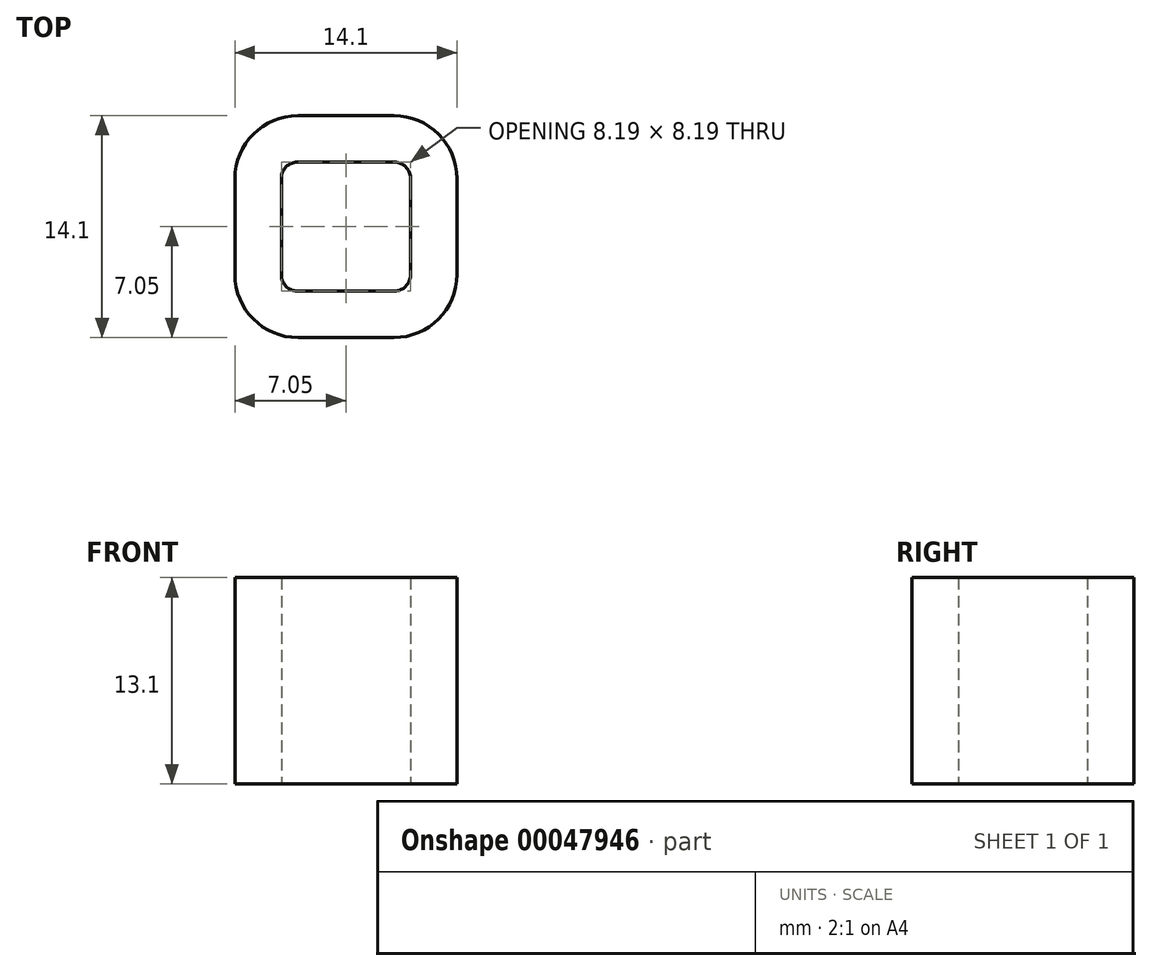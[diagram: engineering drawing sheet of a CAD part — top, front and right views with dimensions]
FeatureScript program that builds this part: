
annotation { "Feature Type Name" : "Feature", "Feature Type Description" : "" }
export const myFeature = defineFeature(function(context is Context, id is Id, definition is map)
    precondition{}
    {
        {
            var Q0;
            Q0=qCreatedBy(makeId("Top.planeOp"),FACE);
            var sketch = newSketch(context, id + "F0", { "sketchPlane" : qUnion([Q0])});
            skLineSegment(sketch, "E0.bottom", {"start": v(-3.8, 3.8) * mm, "end": v(3.8, 3.8) * mm, "construction": true});
            skLineSegment(sketch, "E0.top", {"start": v(-3.8, -3.8) * mm, "end": v(3.8, -3.8) * mm, "construction": true});
            skLineSegment(sketch, "E0.left", {"start": v(-3.8, 3.8) * mm, "end": v(-3.8, -3.8) * mm, "construction": true});
            skLineSegment(sketch, "E0.right", {"start": v(3.8, 3.8) * mm, "end": v(3.8, -3.8) * mm, "construction": true});
            skLineSegment(sketch, "E1.bottom", {"start": v(-7.05, 7.05) * mm, "end": v(7.05, 7.05) * mm, "construction": true});
            skLineSegment(sketch, "E1.top", {"start": v(-7.05, -7.05) * mm, "end": v(7.05, -7.05) * mm, "construction": true});
            skLineSegment(sketch, "E1.left", {"start": v(-7.05, 7.05) * mm, "end": v(-7.05, -7.05) * mm, "construction": true});
            skLineSegment(sketch, "E1.right", {"start": v(7.05, 7.05) * mm, "end": v(7.05, -7.05) * mm, "construction": true});
            skLineSegment(sketch, "E2.bottom", {"start": v(-3.1, 4.1) * mm, "end": v(3.1, 4.1) * mm});
            skLineSegment(sketch, "E2.top", {"start": v(-3.1, -4.1) * mm, "end": v(3.1, -4.1) * mm});
            skLineSegment(sketch, "E2.left", {"start": v(-4.1, 3.1) * mm, "end": v(-4.1, -3.1) * mm});
            skLineSegment(sketch, "E2.right", {"start": v(4.1, 3.1) * mm, "end": v(4.1, -3.1) * mm});
            skPoint(sketch, "E3.visualSharp", {"position": v(-4.1, 4.1) * mm});
            skArc(sketch, "E3.filletArc", {"start": v(-3.1, 4.1) * mm, "mid": v(-3.8, 3.8) * mm, "end": v(-4.1, 3.1) * mm});
            skPoint(sketch, "E4.visualSharp", {"position": v(4.1, 4.1) * mm});
            skArc(sketch, "E4.filletArc", {"start": v(4.1, 3.1) * mm, "mid": v(3.8, 3.8) * mm, "end": v(3.1, 4.1) * mm});
            skPoint(sketch, "E5.visualSharp", {"position": v(4.1, -4.1) * mm});
            skArc(sketch, "E5.filletArc", {"start": v(3.1, -4.1) * mm, "mid": v(3.8, -3.8) * mm, "end": v(4.1, -3.1) * mm});
            skPoint(sketch, "E6.visualSharp", {"position": v(-4.1, -4.1) * mm});
            skArc(sketch, "E6.filletArc", {"start": v(-4.1, -3.1) * mm, "mid": v(-3.8, -3.8) * mm, "end": v(-3.1, -4.1) * mm});
            skLineSegment(sketch, "E7.bottom", {"start": v(-3.05, 7.05) * mm, "end": v(3.05, 7.05) * mm});
            skLineSegment(sketch, "E7.top", {"start": v(-3.05, -7.05) * mm, "end": v(3.05, -7.05) * mm});
            skLineSegment(sketch, "E7.left", {"start": v(-7.05, 3.05) * mm, "end": v(-7.05, -3.05) * mm});
            skLineSegment(sketch, "E7.right", {"start": v(7.05, 3.05) * mm, "end": v(7.05, -3.05) * mm});
            skPoint(sketch, "E8.visualSharp", {"position": v(7.05, 7.05) * mm});
            skArc(sketch, "E8.filletArc", {"start": v(7.05, 3.05) * mm, "mid": v(5.88, 5.88) * mm, "end": v(3.05, 7.05) * mm});
            skPoint(sketch, "E9.visualSharp", {"position": v(-7.05, 7.05) * mm});
            skArc(sketch, "E9.filletArc", {"start": v(-3.05, 7.05) * mm, "mid": v(-5.88, 5.88) * mm, "end": v(-7.05, 3.05) * mm});
            skPoint(sketch, "E10.visualSharp", {"position": v(-7.05, -7.05) * mm});
            skArc(sketch, "E10.filletArc", {"start": v(-7.05, -3.05) * mm, "mid": v(-5.88, -5.88) * mm, "end": v(-3.05, -7.05) * mm});
            skPoint(sketch, "E11.visualSharp", {"position": v(7.05, -7.05) * mm});
            skArc(sketch, "E11.filletArc", {"start": v(3.05, -7.05) * mm, "mid": v(5.88, -5.88) * mm, "end": v(7.05, -3.05) * mm});
            skSolve(sketch);
        }
        {
            var Q0;
            Q0 = qSketchRegion(id + "F0", true);
            extrude(context, id + "F1", {"entities" : qUnion([Q0]), "depth" : 13.1 * mm});
        }
    });
